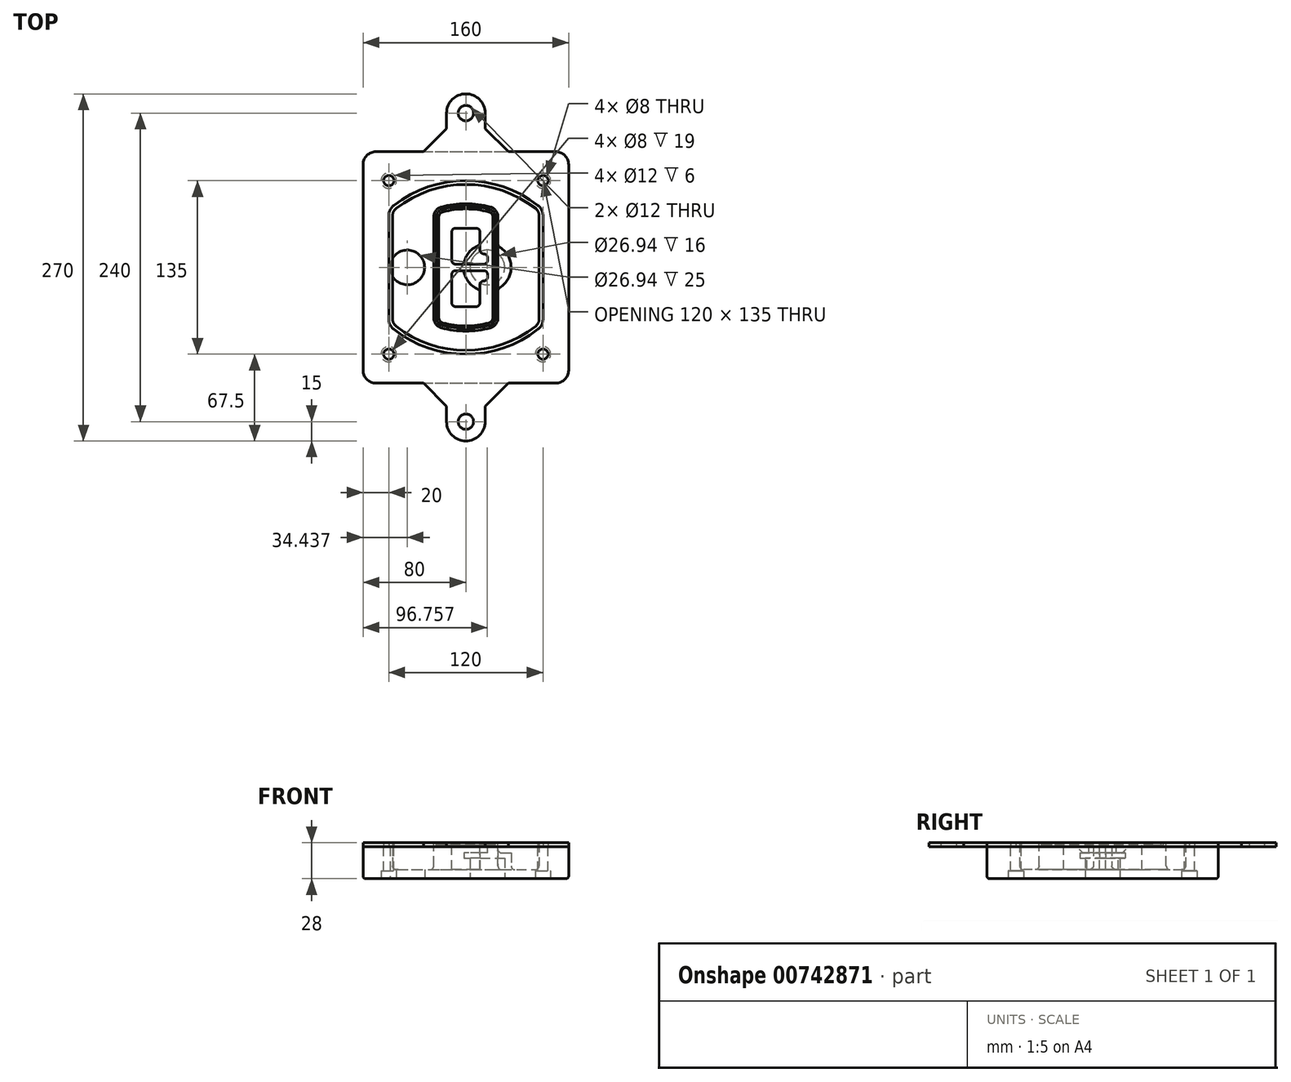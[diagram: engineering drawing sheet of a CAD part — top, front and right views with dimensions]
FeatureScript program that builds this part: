
annotation { "Feature Type Name" : "Feature", "Feature Type Description" : "" }
export const myFeature = defineFeature(function(context is Context, id is Id, definition is map)
    precondition{}
    {
        {
            var Q0;
            Q0=qCreatedBy(makeId("Top.planeOp"),FACE);
            var sketch = newSketch(context, id + "F0", { "sketchPlane" : qUnion([Q0])});
            skPoint(sketch, "E0.rect.middle", {"position": v(0, 0) * mm});
            skLineSegment(sketch, "E1.bottom", {"start": v(-70, -90) * mm, "end": v(70, -90) * mm});
            skLineSegment(sketch, "E1.top", {"start": v(-70, 90) * mm, "end": v(70, 90) * mm});
            skLineSegment(sketch, "E1.left", {"start": v(-80, -80) * mm, "end": v(-80, 80) * mm});
            skLineSegment(sketch, "E1.right", {"start": v(80, -80) * mm, "end": v(80, 80) * mm});
            skLineSegment(sketch, "E2", {"start": v(-80, 90) * mm, "end": v(80, -90) * mm, "construction": true});
            skLineSegment(sketch, "E3", {"start": v(80, 90) * mm, "end": v(-80, -90) * mm, "construction": true});
            skCircle(sketch, "E4", {"center": v(-60, 67.5) * mm, "radius": 4 * mm});
            skCircle(sketch, "E5", {"center": v(60, 67.5) * mm, "radius": 4 * mm});
            skCircle(sketch, "E6", {"center": v(60, -67.5) * mm, "radius": 4 * mm});
            skCircle(sketch, "E7", {"center": v(-60, -67.5) * mm, "radius": 4 * mm});
            skLineSegment(sketch, "E8", {"start": v(-60, 67.5) * mm, "end": v(60, 67.5) * mm, "construction": true});
            skLineSegment(sketch, "E9", {"start": v(60, 67.5) * mm, "end": v(60, -67.5) * mm, "construction": true});
            skLineSegment(sketch, "E10", {"start": v(60, -67.5) * mm, "end": v(-60, -67.5) * mm, "construction": true});
            skLineSegment(sketch, "E11", {"start": v(-60, -67.5) * mm, "end": v(-60, 67.5) * mm, "construction": true});
            skLineSegment(sketch, "E12", {"start": v(-60, 40.3) * mm, "end": v(-60, -40.3) * mm});
            skLineSegment(sketch, "E13", {"start": v(60, 40.3) * mm, "end": v(60, -40.3) * mm});
            skArc(sketch, "E14", {"start": v(56.15, 48.18) * mm, "mid": v(0, 67.5) * mm, "end": v(-56.15, 48.18) * mm});
            skArc(sketch, "E15", {"start": v(-56.15, -48.18) * mm, "mid": v(0, -67.5) * mm, "end": v(56.15, -48.18) * mm});
            skLineSegment(sketch, "E16", {"start": v(-60, 0) * mm, "end": v(60, 0) * mm, "construction": true});
            skPoint(sketch, "E17.visualSharp", {"position": v(-60, -45) * mm});
            skArc(sketch, "E17.filletArc", {"start": v(-60, -40.3) * mm, "mid": v(-58.99, -44.68) * mm, "end": v(-56.15, -48.18) * mm});
            skPoint(sketch, "E18.visualSharp", {"position": v(-60, 45) * mm});
            skArc(sketch, "E18.filletArc", {"start": v(-56.15, 48.18) * mm, "mid": v(-58.99, 44.68) * mm, "end": v(-60, 40.3) * mm});
            skPoint(sketch, "E19.visualSharp", {"position": v(60, 45) * mm});
            skArc(sketch, "E19.filletArc", {"start": v(60, 40.3) * mm, "mid": v(58.99, 44.68) * mm, "end": v(56.15, 48.18) * mm});
            skPoint(sketch, "E20.visualSharp", {"position": v(60, -45) * mm});
            skArc(sketch, "E20.filletArc", {"start": v(56.15, -48.18) * mm, "mid": v(58.99, -44.68) * mm, "end": v(60, -40.3) * mm});
            skPoint(sketch, "E21.visualSharp", {"position": v(-80, 90) * mm});
            skArc(sketch, "E21.filletArc", {"start": v(-70, 90) * mm, "mid": v(-77.07, 87.07) * mm, "end": v(-80, 80) * mm});
            skPoint(sketch, "E22.visualSharp", {"position": v(80, 90) * mm});
            skArc(sketch, "E22.filletArc", {"start": v(80, 80) * mm, "mid": v(77.07, 87.07) * mm, "end": v(70, 90) * mm});
            skPoint(sketch, "E23.visualSharp", {"position": v(80, -90) * mm});
            skArc(sketch, "E23.filletArc", {"start": v(70, -90) * mm, "mid": v(77.07, -87.07) * mm, "end": v(80, -80) * mm});
            skPoint(sketch, "E24.visualSharp", {"position": v(-80, -90) * mm});
            skArc(sketch, "E24.filletArc", {"start": v(-80, -80) * mm, "mid": v(-77.07, -87.07) * mm, "end": v(-70, -90) * mm});
            skArc(sketch, "E25.0", {"start": v(57, 40.3) * mm, "mid": v(56.3, 43.36) * mm, "end": v(54.3, 45.81) * mm});
            skLineSegment(sketch, "E25.1", {"start": v(57, 40.3) * mm, "end": v(57, -40.3) * mm});
            skArc(sketch, "E25.2", {"start": v(54.3, -45.81) * mm, "mid": v(56.3, -43.36) * mm, "end": v(57, -40.3) * mm});
            skArc(sketch, "E25.3", {"start": v(-54.3, -45.81) * mm, "mid": v(0, -64.5) * mm, "end": v(54.3, -45.81) * mm});
            skArc(sketch, "E25.4", {"start": v(-57, -40.3) * mm, "mid": v(-56.3, -43.36) * mm, "end": v(-54.3, -45.81) * mm});
            skArc(sketch, "E25.5", {"start": v(54.3, 45.81) * mm, "mid": v(0, 64.5) * mm, "end": v(-54.3, 45.81) * mm});
            skLineSegment(sketch, "E25.6", {"start": v(-57, 40.3) * mm, "end": v(-57, -40.3) * mm});
            skArc(sketch, "E25.7", {"start": v(-54.3, 45.81) * mm, "mid": v(-56.3, 43.36) * mm, "end": v(-57, 40.3) * mm});
            skArc(sketch, "E26.0", {"start": v(-58.62, 51.33) * mm, "mid": v(-62.58, 46.43) * mm, "end": v(-64, 40.3) * mm});
            skArc(sketch, "E26.1", {"start": v(58.62, 51.33) * mm, "mid": v(0, 71.5) * mm, "end": v(-58.62, 51.33) * mm});
            skArc(sketch, "E26.2", {"start": v(64, 40.3) * mm, "mid": v(62.58, 46.43) * mm, "end": v(58.62, 51.33) * mm});
            skLineSegment(sketch, "E26.3", {"start": v(64, 40.3) * mm, "end": v(64, -40.3) * mm});
            skArc(sketch, "E26.4", {"start": v(58.62, -51.33) * mm, "mid": v(62.58, -46.43) * mm, "end": v(64, -40.3) * mm});
            skLineSegment(sketch, "E26.5", {"start": v(-64, 40.3) * mm, "end": v(-64, -40.3) * mm});
            skArc(sketch, "E26.6", {"start": v(-58.62, -51.33) * mm, "mid": v(0, -71.5) * mm, "end": v(58.62, -51.33) * mm});
            skArc(sketch, "E26.7", {"start": v(-64, -40.3) * mm, "mid": v(-62.58, -46.43) * mm, "end": v(-58.62, -51.33) * mm});
            skSolve(sketch);
        }
        {
            var Q0;
            Q0=makeQuery(id+"F0.imprint","IMPRINT",FACE,{"disambiguationData":[TD([[makeQuery(id+"F0.imprint","IMPRINT",EDGE,{"derivedFrom":sQuery(id+"F0.wireOp",EDGE,"E1.bottom")}),1.0]])]});
            var Q1;
            Q1=makeQuery(id+"F0.imprint","IMPRINT",FACE,{"disambiguationData":[TD([[makeQuery(id+"F0.imprint","IMPRINT",EDGE,{"derivedFrom":sQuery(id+"F0.wireOp",EDGE,"E12")}),1.0]])]});
            var Q2;
            Q2=makeQuery(id+"F0.imprint","IMPRINT",FACE,{"disambiguationData":[TD([[makeQuery(id+"F0.imprint","IMPRINT",EDGE,{"derivedFrom":sQuery(id+"F0.wireOp",EDGE,"E25.0")}),1.0]])]});
            var Q3;
            Q3=makeQuery(id+"F0.imprint","IMPRINT",FACE,{"disambiguationData":[TD([[makeQuery(id+"F0.imprint","IMPRINT",EDGE,{"derivedFrom":sQuery(id+"F0.wireOp",EDGE,"E12")}),-1.0]])]});
            extrude(context, id + "F1", {"entities" : qUnion([Q0, Q1, Q2, Q3]), "oppositeDirection" : true, "depth" : 25 * mm});
        }
        {
            var Q0;
            Q0=makeQuery(id+"F0.imprint","IMPRINT",FACE,{"disambiguationData":[TD([[makeQuery(id+"F0.imprint","IMPRINT",EDGE,{"derivedFrom":sQuery(id+"F0.wireOp",EDGE,"E12")}),1.0]])]});
            extrude(context, id + "F2", {"entities" : qUnion([Q0]), "operationType" : NewBodyOperationType.ADD, "depth" : 3 * mm});
        }
        {
            var Q0;
            Q0=makeQuery(id+"F0.imprint","IMPRINT",FACE,{"disambiguationData":[TD([[makeQuery(id+"F0.imprint","IMPRINT",EDGE,{"derivedFrom":sQuery(id+"F0.wireOp",EDGE,"E25.0")}),1.0]])]});
            extrude(context, id + "F3", {"entities" : qUnion([Q0]), "operationType" : NewBodyOperationType.REMOVE, "oppositeDirection" : true, "depth" : 18 * mm});
        }
        {
            var Q0;
            Q0=makeQuery(id+"F2.opExtrude","CAP_FACE",FACE,{"disambiguationData":[OSD([sQuery(id+"F0.wireOp",EDGE,"E12"),sQuery(id+"F0.wireOp",EDGE,"E13"),sQuery(id+"F0.wireOp",EDGE,"E14"),sQuery(id+"F0.wireOp",EDGE,"E15"),sQuery(id+"F0.wireOp",EDGE,"E17.filletArc"),sQuery(id+"F0.wireOp",EDGE,"E18.filletArc"),sQuery(id+"F0.wireOp",EDGE,"E19.filletArc"),sQuery(id+"F0.wireOp",EDGE,"E20.filletArc"),sQuery(id+"F0.wireOp",EDGE,"E25.0"),sQuery(id+"F0.wireOp",EDGE,"E25.1"),sQuery(id+"F0.wireOp",EDGE,"E25.2"),sQuery(id+"F0.wireOp",EDGE,"E25.3"),sQuery(id+"F0.wireOp",EDGE,"E25.4"),sQuery(id+"F0.wireOp",EDGE,"E25.5"),sQuery(id+"F0.wireOp",EDGE,"E25.6"),sQuery(id+"F0.wireOp",EDGE,"E25.7")])],"isStart":false});
            var sketch = newSketch(context, id + "F4", { "sketchPlane" : qUnion([Q0])});
            skArc(sketch, "E27.0", {"start": v(-19.08, -46.97) * mm, "mid": v(0, -49.5) * mm, "end": v(19.08, -46.97) * mm});
            skArc(sketch, "E28.0", {"start": v(19.08, 46.97) * mm, "mid": v(0, 49.5) * mm, "end": v(-19.08, 46.97) * mm});
            skLineSegment(sketch, "E29", {"start": v(-25, 39.25) * mm, "end": v(-25, -39.25) * mm});
            skLineSegment(sketch, "E30", {"start": v(25, 39.25) * mm, "end": v(25, -39.25) * mm});
            skLineSegment(sketch, "E31", {"start": v(-25, 45.1) * mm, "end": v(25, 45.1) * mm, "construction": true});
            skLineSegment(sketch, "E32", {"start": v(-25, -45.1) * mm, "end": v(25, -45.1) * mm, "construction": true});
            skPoint(sketch, "E33.visualSharp", {"position": v(-25, 45.1) * mm});
            skArc(sketch, "E33.filletArc", {"start": v(-19.08, 46.97) * mm, "mid": v(-23.35, 44.11) * mm, "end": v(-25, 39.25) * mm});
            skPoint(sketch, "E34.visualSharp", {"position": v(25, 45.1) * mm});
            skArc(sketch, "E34.filletArc", {"start": v(25, 39.25) * mm, "mid": v(23.35, 44.11) * mm, "end": v(19.08, 46.97) * mm});
            skPoint(sketch, "E35.visualSharp", {"position": v(25, -45.1) * mm});
            skArc(sketch, "E35.filletArc", {"start": v(19.08, -46.97) * mm, "mid": v(23.35, -44.11) * mm, "end": v(25, -39.25) * mm});
            skPoint(sketch, "E36.visualSharp", {"position": v(-25, -45.1) * mm});
            skArc(sketch, "E36.filletArc", {"start": v(-25, -39.25) * mm, "mid": v(-23.35, -44.11) * mm, "end": v(-19.08, -46.97) * mm});
            skArc(sketch, "E37.0", {"start": v(54.3, 45.81) * mm, "mid": v(0, 64.5) * mm, "end": v(-54.3, 45.81) * mm});
            skArc(sketch, "E37.1", {"start": v(-54.3, 45.81) * mm, "mid": v(-56.3, 43.36) * mm, "end": v(-57, 40.3) * mm});
            skLineSegment(sketch, "E37.2", {"start": v(-57, 40.3) * mm, "end": v(-57, -40.3) * mm});
            skArc(sketch, "E37.3", {"start": v(-57, -40.3) * mm, "mid": v(-56.3, -43.36) * mm, "end": v(-54.3, -45.81) * mm});
            skArc(sketch, "E37.4", {"start": v(-54.3, -45.81) * mm, "mid": v(0, -64.5) * mm, "end": v(54.3, -45.81) * mm});
            skArc(sketch, "E37.5", {"start": v(54.3, -45.81) * mm, "mid": v(56.3, -43.36) * mm, "end": v(57, -40.3) * mm});
            skLineSegment(sketch, "E37.6", {"start": v(57, 40.3) * mm, "end": v(57, -40.3) * mm});
            skArc(sketch, "E37.7", {"start": v(57, 40.3) * mm, "mid": v(56.3, 43.36) * mm, "end": v(54.3, 45.81) * mm});
            skLineSegment(sketch, "E38.0", {"start": v(23, 39.25) * mm, "end": v(23, -39.25) * mm});
            skArc(sketch, "E38.1", {"start": v(18.56, -45.04) * mm, "mid": v(21.76, -42.9) * mm, "end": v(23, -39.25) * mm});
            skArc(sketch, "E38.2", {"start": v(-18.56, -45.04) * mm, "mid": v(0, -47.5) * mm, "end": v(18.56, -45.04) * mm});
            skArc(sketch, "E38.3", {"start": v(-23, -39.25) * mm, "mid": v(-21.76, -42.9) * mm, "end": v(-18.56, -45.04) * mm});
            skLineSegment(sketch, "E38.4", {"start": v(-23, 39.25) * mm, "end": v(-23, -39.25) * mm});
            skArc(sketch, "E38.5", {"start": v(23, 39.25) * mm, "mid": v(21.76, 42.9) * mm, "end": v(18.56, 45.04) * mm});
            skArc(sketch, "E38.6", {"start": v(-18.56, 45.04) * mm, "mid": v(-21.76, 42.9) * mm, "end": v(-23, 39.25) * mm});
            skArc(sketch, "E38.7", {"start": v(18.56, 45.04) * mm, "mid": v(0, 47.5) * mm, "end": v(-18.56, 45.04) * mm});
            skArc(sketch, "E39.0", {"start": v(21, 39.25) * mm, "mid": v(20.18, 41.68) * mm, "end": v(18.04, 43.1) * mm});
            skLineSegment(sketch, "E39.1", {"start": v(21, 39.25) * mm, "end": v(21, -39.25) * mm});
            skArc(sketch, "E39.2", {"start": v(18.04, -43.1) * mm, "mid": v(20.18, -41.68) * mm, "end": v(21, -39.25) * mm});
            skArc(sketch, "E39.3", {"start": v(-18.04, -43.1) * mm, "mid": v(0, -45.5) * mm, "end": v(18.04, -43.1) * mm});
            skArc(sketch, "E39.4", {"start": v(-21, -39.25) * mm, "mid": v(-20.18, -41.68) * mm, "end": v(-18.04, -43.1) * mm});
            skArc(sketch, "E39.5", {"start": v(18.04, 43.1) * mm, "mid": v(0, 45.5) * mm, "end": v(-18.04, 43.1) * mm});
            skLineSegment(sketch, "E39.6", {"start": v(-21, 39.25) * mm, "end": v(-21, -39.25) * mm});
            skArc(sketch, "E39.7", {"start": v(-18.04, 43.1) * mm, "mid": v(-20.18, 41.68) * mm, "end": v(-21, 39.25) * mm});
            skLineSegment(sketch, "E40", {"start": v(-25, 0) * mm, "end": v(25, 0) * mm, "construction": true});
            skLineSegment(sketch, "E41", {"start": v(-11, 5.5) * mm, "end": v(-11, 27.5) * mm});
            skLineSegment(sketch, "E42", {"start": v(-8, 30.5) * mm, "end": v(8, 30.5) * mm});
            skLineSegment(sketch, "E43", {"start": v(11, 27.5) * mm, "end": v(11, 13.5) * mm});
            skLineSegment(sketch, "E44", {"start": v(14, 10.5) * mm, "end": v(14, 10.5) * mm});
            skLineSegment(sketch, "E45", {"start": v(17, 7.5) * mm, "end": v(17, 5.5) * mm});
            skLineSegment(sketch, "E46", {"start": v(14, 2.5) * mm, "end": v(-8, 2.5) * mm});
            skPoint(sketch, "E47.visualSharp", {"position": v(-11, 30.5) * mm});
            skArc(sketch, "E47.filletArc", {"start": v(-8, 30.5) * mm, "mid": v(-10.12, 29.62) * mm, "end": v(-11, 27.5) * mm});
            skPoint(sketch, "E48.visualSharp", {"position": v(11, 30.5) * mm});
            skArc(sketch, "E48.filletArc", {"start": v(11, 27.5) * mm, "mid": v(10.12, 29.62) * mm, "end": v(8, 30.5) * mm});
            skPoint(sketch, "E49.visualSharp", {"position": v(11, 10.5) * mm});
            skArc(sketch, "E49.filletArc", {"start": v(11, 13.5) * mm, "mid": v(11.88, 11.38) * mm, "end": v(14, 10.5) * mm});
            skPoint(sketch, "E50.visualSharp", {"position": v(17, 10.5) * mm});
            skArc(sketch, "E50.filletArc", {"start": v(17, 7.5) * mm, "mid": v(16.12, 9.62) * mm, "end": v(14, 10.5) * mm});
            skPoint(sketch, "E51.visualSharp", {"position": v(17, 2.5) * mm});
            skArc(sketch, "E51.filletArc", {"start": v(14, 2.5) * mm, "mid": v(16.12, 3.38) * mm, "end": v(17, 5.5) * mm});
            skPoint(sketch, "E52.visualSharp", {"position": v(-11, 2.5) * mm});
            skArc(sketch, "E52.filletArc", {"start": v(-11, 5.5) * mm, "mid": v(-10.12, 3.38) * mm, "end": v(-8, 2.5) * mm});
            skLineSegment(sketch, "E53.0.MirrorCS", {"start": v(14, -2.5) * mm, "end": v(-8, -2.5) * mm});
            skArc(sketch, "E54.0.MirrorCS", {"start": v(-11, -5.5) * mm, "mid": v(-10.12, -3.38) * mm, "end": v(-8, -2.5) * mm});
            skLineSegment(sketch, "E55.0.MirrorCS", {"start": v(-11, -5.5) * mm, "end": v(-11, -27.5) * mm});
            skArc(sketch, "E56.0.MirrorCS", {"start": v(-8, -30.5) * mm, "mid": v(-10.12, -29.62) * mm, "end": v(-11, -27.5) * mm});
            skLineSegment(sketch, "E57.0.MirrorCS", {"start": v(-8, -30.5) * mm, "end": v(8, -30.5) * mm});
            skArc(sketch, "E58.0.MirrorCS", {"start": v(11, -27.5) * mm, "mid": v(10.12, -29.62) * mm, "end": v(8, -30.5) * mm});
            skLineSegment(sketch, "E59.0.MirrorCS", {"start": v(11, -27.5) * mm, "end": v(11, -13.5) * mm});
            skArc(sketch, "E60.0.MirrorCS", {"start": v(11, -13.5) * mm, "mid": v(11.88, -11.38) * mm, "end": v(14, -10.5) * mm});
            skArc(sketch, "E61.0.MirrorCS", {"start": v(17, -7.5) * mm, "mid": v(16.12, -9.62) * mm, "end": v(14, -10.5) * mm});
            skLineSegment(sketch, "E62.0.MirrorCS", {"start": v(17, -7.5) * mm, "end": v(17, -5.5) * mm});
            skArc(sketch, "E63.0.MirrorCS", {"start": v(14, -2.5) * mm, "mid": v(16.12, -3.38) * mm, "end": v(17, -5.5) * mm});
            skSolve(sketch);
        }
        {
            var Q0;
            Q0=makeQuery(id+"F4.imprint","IMPRINT",FACE,{"disambiguationData":[TD([[makeQuery(id+"F4.imprint","IMPRINT",EDGE,{"derivedFrom":sQuery(id+"F4.wireOp",EDGE,"E27.0")}),1.0]])]});
            var Q1;
            Q1=makeQuery(id+"F4.imprint","IMPRINT",FACE,{"disambiguationData":[TD([[makeQuery(id+"F4.imprint","IMPRINT",EDGE,{"derivedFrom":sQuery(id+"F4.wireOp",EDGE,"E38.0")}),-1.0]])]});
            var Q2;
            Q2=makeQuery(id+"F4.imprint","IMPRINT",FACE,{"disambiguationData":[TD([[makeQuery(id+"F4.imprint","IMPRINT",EDGE,{"derivedFrom":sQuery(id+"F4.wireOp",EDGE,"E39.0")}),1.0]])]});
            extrude(context, id + "F5", {"entities" : qUnion([Q0, Q1, Q2]), "operationType" : NewBodyOperationType.ADD, "endBound" : BoundingType.UP_TO_NEXT, "oppositeDirection" : true, "depth" : 25 * mm});
        }
        {
            var Q0;
            Q0=makeQuery(id+"F4.imprint","IMPRINT",FACE,{"disambiguationData":[TD([[makeQuery(id+"F4.imprint","IMPRINT",EDGE,{"derivedFrom":sQuery(id+"F4.wireOp",EDGE,"E38.0")}),-1.0]])]});
            extrude(context, id + "F6", {"entities" : qUnion([Q0]), "operationType" : NewBodyOperationType.REMOVE, "oppositeDirection" : true, "depth" : 2 * mm});
        }
        {
            var Q0;
            Q0=makeQuery(id+"F1.opExtrude","CAP_FACE",FACE,{"disambiguationData":[OSD([sQuery(id+"F0.wireOp",EDGE,"E1.bottom"),sQuery(id+"F0.wireOp",EDGE,"E1.top"),sQuery(id+"F0.wireOp",EDGE,"E1.left"),sQuery(id+"F0.wireOp",EDGE,"E1.right"),sQuery(id+"F0.wireOp",EDGE,"E4"),sQuery(id+"F0.wireOp",EDGE,"E5"),sQuery(id+"F0.wireOp",EDGE,"E6"),sQuery(id+"F0.wireOp",EDGE,"E7"),sQuery(id+"F0.wireOp",EDGE,"E21.filletArc"),sQuery(id+"F0.wireOp",EDGE,"E22.filletArc"),sQuery(id+"F0.wireOp",EDGE,"E23.filletArc"),sQuery(id+"F0.wireOp",EDGE,"E24.filletArc")])],"isStart":false});
            var sketch = newSketch(context, id + "F7", { "sketchPlane" : qUnion([Q0])});
            skCircle(sketch, "E64", {"center": v(16.76, 0) * mm, "radius": 13.47 * mm});
            skCircle(sketch, "E65", {"center": v(-45.56, 0) * mm, "radius": 13.47 * mm});
            skLineSegment(sketch, "E66", {"start": v(80, 0) * mm, "end": v(-80, 0) * mm});
            skCircle(sketch, "E67", {"center": v(16.76, 0) * mm, "radius": 18.47 * mm});
            skCircle(sketch, "E68", {"center": v(60, -67.5) * mm, "radius": 6 * mm});
            skCircle(sketch, "E69", {"center": v(-60, -67.5) * mm, "radius": 6 * mm});
            skCircle(sketch, "E70", {"center": v(-60, 67.5) * mm, "radius": 6 * mm});
            skCircle(sketch, "E71", {"center": v(60, 67.5) * mm, "radius": 6 * mm});
            skSolve(sketch);
        }
        {
            var Q0;
            {var subQ1=sQuery(id+"F7.wireOp",EDGE,"E66");var subQ4=sQuery(id+"F7.wireOp",EDGE,"E64");var subQ6=makeQuery(id+"F7.imprint","INTERSECT",VERTEX,{"disambiguationData":[OD(0.0)],"derivedFrom":[subQ4,subQ1]});Q0=makeQuery(id+"F7.imprint","IMPRINT",FACE,{"disambiguationData":[TD([[makeQuery(id+"F7.imprint","IMPRINT",EDGE,{"disambiguationData":[TD([[subQ6,-1.0]])],"derivedFrom":subQ4}),-1.0]])]});}
            var Q1;
            {var subQ0=sQuery(id+"F7.wireOp",EDGE,"E66");var subQ1=sQuery(id+"F7.wireOp",EDGE,"E64");var subQ3=makeQuery(id+"F7.imprint","INTERSECT",VERTEX,{"disambiguationData":[OD(0.0)],"derivedFrom":[subQ1,subQ0]});Q1=makeQuery(id+"F7.imprint","IMPRINT",FACE,{"disambiguationData":[TD([[makeQuery(id+"F7.imprint","IMPRINT",EDGE,{"disambiguationData":[TD([[subQ3,-1.0]])],"derivedFrom":subQ1}),1.0]])]});}
            var Q2;
            {var subQ0=sQuery(id+"F7.wireOp",EDGE,"E66");var subQ1=sQuery(id+"F7.wireOp",EDGE,"E64");var subQ3=makeQuery(id+"F7.imprint","INTERSECT",VERTEX,{"disambiguationData":[OD(0.0)],"derivedFrom":[subQ1,subQ0]});Q2=makeQuery(id+"F7.imprint","IMPRINT",FACE,{"disambiguationData":[TD([[makeQuery(id+"F7.imprint","IMPRINT",EDGE,{"disambiguationData":[TD([[subQ3,1.0]])],"derivedFrom":subQ1}),1.0]])]});}
            var Q3;
            {var subQ1=sQuery(id+"F7.wireOp",EDGE,"E66");var subQ4=sQuery(id+"F7.wireOp",EDGE,"E64");var subQ6=makeQuery(id+"F7.imprint","INTERSECT",VERTEX,{"disambiguationData":[OD(0.0)],"derivedFrom":[subQ4,subQ1]});Q3=makeQuery(id+"F7.imprint","IMPRINT",FACE,{"disambiguationData":[TD([[makeQuery(id+"F7.imprint","IMPRINT",EDGE,{"disambiguationData":[TD([[subQ6,1.0]])],"derivedFrom":subQ4}),-1.0]])]});}
            extrude(context, id + "F8", {"entities" : qUnion([Q0, Q1, Q2, Q3]), "operationType" : NewBodyOperationType.ADD, "oppositeDirection" : true, "depth" : 20 * mm});
        }
        {
            var Q0;
            {var subQ0=sQuery(id+"F7.wireOp",EDGE,"E66");var subQ1=sQuery(id+"F7.wireOp",EDGE,"E64");var subQ3=makeQuery(id+"F7.imprint","INTERSECT",VERTEX,{"disambiguationData":[OD(0.0)],"derivedFrom":[subQ1,subQ0]});Q0=makeQuery(id+"F7.imprint","IMPRINT",FACE,{"disambiguationData":[TD([[makeQuery(id+"F7.imprint","IMPRINT",EDGE,{"disambiguationData":[TD([[subQ3,-1.0]])],"derivedFrom":subQ1}),1.0]])]});}
            var Q1;
            {var subQ0=sQuery(id+"F7.wireOp",EDGE,"E66");var subQ1=sQuery(id+"F7.wireOp",EDGE,"E64");var subQ3=makeQuery(id+"F7.imprint","INTERSECT",VERTEX,{"disambiguationData":[OD(0.0)],"derivedFrom":[subQ1,subQ0]});Q1=makeQuery(id+"F7.imprint","IMPRINT",FACE,{"disambiguationData":[TD([[makeQuery(id+"F7.imprint","IMPRINT",EDGE,{"disambiguationData":[TD([[subQ3,1.0]])],"derivedFrom":subQ1}),1.0]])]});}
            extrude(context, id + "F9", {"entities" : qUnion([Q0, Q1]), "operationType" : NewBodyOperationType.REMOVE, "oppositeDirection" : true, "depth" : 16 * mm});
        }
        {
            var Q0;
            {var subQ0=sQuery(id+"F7.wireOp",EDGE,"E66");var subQ1=sQuery(id+"F7.wireOp",EDGE,"E65");var subQ3=makeQuery(id+"F7.imprint","INTERSECT",VERTEX,{"disambiguationData":[OD(0.0)],"derivedFrom":[subQ1,subQ0]});Q0=makeQuery(id+"F7.imprint","IMPRINT",FACE,{"disambiguationData":[TD([[makeQuery(id+"F7.imprint","IMPRINT",EDGE,{"disambiguationData":[TD([[subQ3,-1.0]])],"derivedFrom":subQ1}),1.0]])]});}
            var Q1;
            {var subQ0=sQuery(id+"F7.wireOp",EDGE,"E66");var subQ1=sQuery(id+"F7.wireOp",EDGE,"E65");var subQ3=makeQuery(id+"F7.imprint","INTERSECT",VERTEX,{"disambiguationData":[OD(0.0)],"derivedFrom":[subQ1,subQ0]});Q1=makeQuery(id+"F7.imprint","IMPRINT",FACE,{"disambiguationData":[TD([[makeQuery(id+"F7.imprint","IMPRINT",EDGE,{"disambiguationData":[TD([[subQ3,1.0]])],"derivedFrom":subQ1}),1.0]])]});}
            extrude(context, id + "F10", {"entities" : qUnion([Q0, Q1]), "operationType" : NewBodyOperationType.REMOVE, "oppositeDirection" : true, "depth" : 25 * mm});
        }
        {
            var Q0;
            Q0=makeQuery(id+"F7.imprint","IMPRINT",FACE,{"disambiguationData":[TD([[makeQuery(id+"F7.imprint","IMPRINT",EDGE,{"derivedFrom":sQuery(id+"F7.wireOp",EDGE,"E68")}),1.0]])]});
            var Q1;
            Q1=makeQuery(id+"F7.imprint","IMPRINT",FACE,{"disambiguationData":[TD([[makeQuery(id+"F7.imprint","IMPRINT",EDGE,{"derivedFrom":makeQuery(id+"F1.opExtrude","CAP_EDGE",EDGE,{"disambiguationData":[OSD([sQuery(id+"F0.wireOp",EDGE,"E5")])],"isStart":false})}),-1.0]])]});
            var Q2;
            Q2=makeQuery(id+"F7.imprint","IMPRINT",FACE,{"disambiguationData":[TD([[makeQuery(id+"F7.imprint","IMPRINT",EDGE,{"derivedFrom":sQuery(id+"F7.wireOp",EDGE,"E69")}),1.0]])]});
            var Q3;
            Q3=makeQuery(id+"F7.imprint","IMPRINT",FACE,{"disambiguationData":[TD([[makeQuery(id+"F7.imprint","IMPRINT",EDGE,{"derivedFrom":makeQuery(id+"F1.opExtrude","CAP_EDGE",EDGE,{"disambiguationData":[OSD([sQuery(id+"F0.wireOp",EDGE,"E4")])],"isStart":false})}),-1.0]])]});
            var Q4;
            Q4=makeQuery(id+"F7.imprint","IMPRINT",FACE,{"disambiguationData":[TD([[makeQuery(id+"F7.imprint","IMPRINT",EDGE,{"derivedFrom":sQuery(id+"F7.wireOp",EDGE,"E70")}),1.0]])]});
            var Q5;
            Q5=makeQuery(id+"F7.imprint","IMPRINT",FACE,{"disambiguationData":[TD([[makeQuery(id+"F7.imprint","IMPRINT",EDGE,{"derivedFrom":makeQuery(id+"F1.opExtrude","CAP_EDGE",EDGE,{"disambiguationData":[OSD([sQuery(id+"F0.wireOp",EDGE,"E7")])],"isStart":false})}),-1.0]])]});
            var Q6;
            Q6=makeQuery(id+"F7.imprint","IMPRINT",FACE,{"disambiguationData":[TD([[makeQuery(id+"F7.imprint","IMPRINT",EDGE,{"derivedFrom":sQuery(id+"F7.wireOp",EDGE,"E71")}),1.0]])]});
            var Q7;
            Q7=makeQuery(id+"F7.imprint","IMPRINT",FACE,{"disambiguationData":[TD([[makeQuery(id+"F7.imprint","IMPRINT",EDGE,{"derivedFrom":makeQuery(id+"F1.opExtrude","CAP_EDGE",EDGE,{"disambiguationData":[OSD([sQuery(id+"F0.wireOp",EDGE,"E6")])],"isStart":false})}),-1.0]])]});
            extrude(context, id + "F11", {"entities" : qUnion([Q0, Q1, Q2, Q3, Q4, Q5, Q6, Q7]), "operationType" : NewBodyOperationType.REMOVE, "oppositeDirection" : true, "depth" : 6 * mm});
        }
        {
            var Q0;
            Q0=makeQuery(id+"F9.boolean.opBoolean","COPY",FACE,{"derivedFrom":makeQuery(id+"F9.opExtrude","CAP_FACE",FACE,{"disambiguationData":[OSD([sQuery(id+"F7.wireOp",EDGE,"E64")])],"isStart":false})});
            var sketch = newSketch(context, id + "F12", { "sketchPlane" : qUnion([Q0])});
            skArc(sketch, "E72.0", {"start": v(11, 17.55) * mm, "mid": v(2.57, 11.82) * mm, "end": v(-1.54, 2.5) * mm});
            skArc(sketch, "E72.1", {"start": v(-1.54, -2.5) * mm, "mid": v(2.57, -11.82) * mm, "end": v(11, -17.55) * mm});
            skLineSegment(sketch, "E73", {"start": v(-1.54, -2.5) * mm, "end": v(14, -2.5) * mm});
            skLineSegment(sketch, "E74.0", {"start": v(14, 2.5) * mm, "end": v(-1.54, 2.5) * mm});
            skArc(sketch, "E74.1", {"start": v(14, 2.5) * mm, "mid": v(16.12, 3.38) * mm, "end": v(17, 5.5) * mm});
            skLineSegment(sketch, "E74.2", {"start": v(17, 7.5) * mm, "end": v(17, 5.5) * mm});
            skArc(sketch, "E74.3", {"start": v(17, 7.5) * mm, "mid": v(16.12, 9.62) * mm, "end": v(14, 10.5) * mm});
            skArc(sketch, "E74.4", {"start": v(11, 13.5) * mm, "mid": v(11.88, 11.38) * mm, "end": v(14, 10.5) * mm});
            skLineSegment(sketch, "E74.5", {"start": v(11, 17.55) * mm, "end": v(11, 13.5) * mm});
            skLineSegment(sketch, "E74.7", {"start": v(14, -2.5) * mm, "end": v(-1.54, -2.5) * mm});
            skArc(sketch, "E74.8", {"start": v(14, -2.5) * mm, "mid": v(16.12, -3.38) * mm, "end": v(17, -5.5) * mm});
            skLineSegment(sketch, "E74.9", {"start": v(17, -7.5) * mm, "end": v(17, -5.5) * mm});
            skArc(sketch, "E74.10", {"start": v(17, -7.5) * mm, "mid": v(16.12, -9.62) * mm, "end": v(14, -10.5) * mm});
            skArc(sketch, "E74.11", {"start": v(11, -13.5) * mm, "mid": v(11.88, -11.38) * mm, "end": v(14, -10.5) * mm});
            skLineSegment(sketch, "E74.12", {"start": v(11, -17.55) * mm, "end": v(11, -13.5) * mm});
            skPoint(sketch, "E75.orphan", {"position": v(11, -27.5) * mm});
            skPoint(sketch, "E76.orphan", {"position": v(-8, -2.5) * mm});
            skPoint(sketch, "E77.orphan", {"position": v(-8, 2.5) * mm});
            skPoint(sketch, "E78.orphan", {"position": v(11, 27.5) * mm});
            skSolve(sketch);
        }
        {
            var Q0;
            {var subQ7=sQuery(id+"F12.wireOp",EDGE,"E72.0");var subQ14=sQuery(id+"F12.wireOp",EDGE,"E72.1");var subQ16=sQuery(id+"F12.wireOp",EDGE,"E74.1");var subQ18=sQuery(id+"F12.wireOp",EDGE,"E74.8");Q0=qUnion([makeQuery(id+"F12.imprint","IMPRINT",FACE,{"disambiguationData":[TD([[makeQuery(id+"F12.imprint","IMPRINT",EDGE,{"derivedFrom":subQ7}),1.0]])]}),makeQuery(id+"F12.imprint","IMPRINT",FACE,{"disambiguationData":[TD([[makeQuery(id+"F12.imprint","IMPRINT",EDGE,{"derivedFrom":subQ14}),1.0]])]}),makeQuery(id+"F12.imprint","IMPRINT",FACE,{"disambiguationData":[TD([[makeQuery(id+"F12.imprint","IMPRINT",EDGE,{"derivedFrom":subQ16}),1.0]])]}),makeQuery(id+"F12.imprint","IMPRINT",FACE,{"disambiguationData":[TD([[makeQuery(id+"F12.imprint","IMPRINT",EDGE,{"derivedFrom":subQ18}),-1.0]])]})]);}
            var Q1;
            Q1=makeQuery(id+"F5.boolean.opBoolean","SPLIT",FACE,{"disambiguationData":[TD([makeQuery(id+"F5.opExtrude","SWEPT_FACE",FACE,{"disambiguationData":[OSD([sQuery(id+"F4.wireOp",EDGE,"E41")])]})])],"derivedFrom":makeQuery(id+"F3.boolean.opBoolean","COPY",FACE,{"derivedFrom":makeQuery(id+"F3.opExtrude","CAP_FACE",FACE,{"disambiguationData":[OSD([sQuery(id+"F0.wireOp",EDGE,"E25.0"),sQuery(id+"F0.wireOp",EDGE,"E25.1"),sQuery(id+"F0.wireOp",EDGE,"E25.2"),sQuery(id+"F0.wireOp",EDGE,"E25.3"),sQuery(id+"F0.wireOp",EDGE,"E25.4"),sQuery(id+"F0.wireOp",EDGE,"E25.5"),sQuery(id+"F0.wireOp",EDGE,"E25.6"),sQuery(id+"F0.wireOp",EDGE,"E25.7")])],"isStart":false})})});
            extrude(context, id + "F13", {"entities" : qUnion([Q0]), "operationType" : NewBodyOperationType.REMOVE, "endBound" : BoundingType.UP_TO_SURFACE, "endBoundEntityFace" : qUnion([Q1]), "depth" : 25 * mm});
        }
        {
            var Q0;
            Q0=makeQuery(id+"F3.boolean.opBoolean","COPY",EDGE,{"derivedFrom":makeQuery(id+"F3.opExtrude","CAP_EDGE",EDGE,{"disambiguationData":[OSD([sQuery(id+"F0.wireOp",EDGE,"E25.6")])],"isStart":false})});
            var Q1;
            Q1=makeQuery(id+"F8.boolean.opBoolean","INTERSECT",EDGE,{"derivedFrom":[makeQuery(id+"F5.opExtrude","SWEPT_FACE",FACE,{"disambiguationData":[OSD([sQuery(id+"F4.wireOp",EDGE,"E30")])]}),makeQuery(id+"F8.opExtrude","CAP_FACE",FACE,{"disambiguationData":[OSD([sQuery(id+"F7.wireOp",EDGE,"E67")])],"isStart":false})]});
            var Q2;
            Q2=makeQuery(id+"F8.boolean.opBoolean","INTERSECT",EDGE,{"disambiguationData":[OD(1.0)],"derivedFrom":[makeQuery(id+"F5.opExtrude","SWEPT_FACE",FACE,{"disambiguationData":[OSD([sQuery(id+"F4.wireOp",EDGE,"E30")])]}),makeQuery(id+"F8.opExtrude","SWEPT_FACE",FACE,{"disambiguationData":[OSD([sQuery(id+"F7.wireOp",EDGE,"E67")])]})]});
            var Q3;
            {var subQ0=sQuery(id+"F4.wireOp",EDGE,"E30");Q3=makeQuery(id+"F8.boolean.opBoolean","SPLIT",EDGE,{"disambiguationData":[TD([makeQuery(id+"F5.opExtrude","SWEPT_FACE",FACE,{"disambiguationData":[OSD([sQuery(id+"F4.wireOp",EDGE,"E35.filletArc")])]})])],"derivedFrom":makeQuery(id+"F5.opExtrude","CAP_EDGE",EDGE,{"disambiguationData":[OSD([subQ0])],"isStart":false})});}
            var Q4;
            {var subQ0=sQuery(id+"F0.wireOp",EDGE,"E25.7");var subQ1=sQuery(id+"F0.wireOp",EDGE,"E25.1");var subQ2=sQuery(id+"F0.wireOp",EDGE,"E25.6");var subQ3=sQuery(id+"F0.wireOp",EDGE,"E25.5");var subQ4=sQuery(id+"F0.wireOp",EDGE,"E25.4");var subQ5=sQuery(id+"F0.wireOp",EDGE,"E25.0");var subQ6=sQuery(id+"F0.wireOp",EDGE,"E25.2");var subQ7=sQuery(id+"F0.wireOp",EDGE,"E25.3");Q4=makeQuery(id+"F8.boolean.opBoolean","INTERSECT",EDGE,{"derivedFrom":[makeQuery(id+"F5.boolean.opBoolean","SPLIT",FACE,{"disambiguationData":[TD([makeQuery(id+"F2.opExtrude","SWEPT_FACE",FACE,{"disambiguationData":[OSD([subQ5])]})])],"derivedFrom":makeQuery(id+"F3.boolean.opBoolean","COPY",FACE,{"derivedFrom":makeQuery(id+"F3.opExtrude","CAP_FACE",FACE,{"disambiguationData":[OSD([subQ5,subQ1,subQ6,subQ7,subQ4,subQ3,subQ2,subQ0])],"isStart":false})})}),makeQuery(id+"F8.opExtrude","SWEPT_FACE",FACE,{"disambiguationData":[OSD([sQuery(id+"F7.wireOp",EDGE,"E67")])]})]});}
            var Q5;
            Q5=makeQuery(id+"F8.boolean.opBoolean","INTERSECT",EDGE,{"disambiguationData":[OD(0.0)],"derivedFrom":[makeQuery(id+"F5.opExtrude","SWEPT_FACE",FACE,{"disambiguationData":[OSD([sQuery(id+"F4.wireOp",EDGE,"E30")])]}),makeQuery(id+"F8.opExtrude","SWEPT_FACE",FACE,{"disambiguationData":[OSD([sQuery(id+"F7.wireOp",EDGE,"E67")])]})]});
            fillet(context, id + "F14", {"entities" : qUnion([Q0, Q1, Q2, Q3, Q4, Q5]), "radius" : 3 * mm, "tangentPropagation" : true, "allowEdgeOverflow" : false});
        }
        {
            var Q0;
            Q0=makeQuery(id+"F1.opExtrude","CAP_EDGE",EDGE,{"disambiguationData":[OSD([sQuery(id+"F0.wireOp",EDGE,"E1.bottom")])],"isStart":false});
            fillet(context, id + "F15", {"entities" : qUnion([Q0]), "radius" : 2 * mm, "tangentPropagation" : true, "allowEdgeOverflow" : false});
        }
        {
            var Q0;
            {var subQ0=sQuery(id+"F0.wireOp",EDGE,"E21.filletArc");var subQ1=sQuery(id+"F0.wireOp",EDGE,"E7");var subQ2=sQuery(id+"F0.wireOp",EDGE,"E6");var subQ3=sQuery(id+"F0.wireOp",EDGE,"E5");var subQ4=sQuery(id+"F0.wireOp",EDGE,"E4");var subQ5=sQuery(id+"F0.wireOp",EDGE,"E22.filletArc");var subQ6=sQuery(id+"F0.wireOp",EDGE,"E1.bottom");var subQ7=sQuery(id+"F0.wireOp",EDGE,"E1.right");var subQ8=sQuery(id+"F0.wireOp",EDGE,"E1.top");var subQ9=sQuery(id+"F0.wireOp",EDGE,"E1.left");var subQ10=sQuery(id+"F0.wireOp",EDGE,"E23.filletArc");var subQ11=sQuery(id+"F0.wireOp",EDGE,"E24.filletArc");Q0=makeQuery(id+"F2.boolean.opBoolean","SPLIT",FACE,{"disambiguationData":[TD([makeQuery(id+"F1.opExtrude","SWEPT_FACE",FACE,{"disambiguationData":[OSD([subQ6])]})])],"derivedFrom":makeQuery(id+"F1.opExtrude","CAP_FACE",FACE,{"disambiguationData":[OSD([subQ6,subQ8,subQ9,subQ7,subQ4,subQ3,subQ2,subQ1,subQ0,subQ5,subQ10,subQ11])],"isStart":true})});}
            var sketch = newSketch(context, id + "F16", { "sketchPlane" : qUnion([Q0])});
            skLineSegment(sketch, "E79", {"start": v(-33, 90) * mm, "end": v(-15, 108) * mm});
            skLineSegment(sketch, "E80", {"start": v(-15, 108) * mm, "end": v(-15, 120) * mm});
            skLineSegment(sketch, "E81", {"start": v(33, 90) * mm, "end": v(15, 108) * mm});
            skLineSegment(sketch, "E82", {"start": v(15, 108) * mm, "end": v(15, 120) * mm});
            skArc(sketch, "E83", {"start": v(15, 120) * mm, "mid": v(0, 135) * mm, "end": v(-15, 120) * mm});
            skCircle(sketch, "E84", {"center": v(0, 120) * mm, "radius": 6 * mm});
            skLineSegment(sketch, "E85", {"start": v(0, 90) * mm, "end": v(0, 120) * mm, "construction": true});
            skLineSegment(sketch, "E86", {"start": v(-80, 0) * mm, "end": v(80, 0) * mm, "construction": true});
            skLineSegment(sketch, "E87.MirrorCS", {"start": v(-33, -90) * mm, "end": v(-15, -108) * mm});
            skLineSegment(sketch, "E88.MirrorCS", {"start": v(-15, -108) * mm, "end": v(-15, -120) * mm});
            skArc(sketch, "E89.MirrorCS", {"start": v(15, -120) * mm, "mid": v(0, -135) * mm, "end": v(-15, -120) * mm});
            skLineSegment(sketch, "E90.MirrorCS", {"start": v(15, -108) * mm, "end": v(15, -120) * mm});
            skLineSegment(sketch, "E91.MirrorCS", {"start": v(33, -90) * mm, "end": v(15, -108) * mm});
            skCircle(sketch, "E92.MirrorC", {"center": v(0, -120) * mm, "radius": 6 * mm});
            skLineSegment(sketch, "E93.MirrorCS", {"start": v(0, -90) * mm, "end": v(0, -120) * mm, "construction": true});
            skSolve(sketch);
        }
        {
            var Q0;
            Q0=makeQuery(id+"F16.imprint","IMPRINT",FACE,{"disambiguationData":[TD([[makeQuery(id+"F16.imprint","IMPRINT",EDGE,{"derivedFrom":sQuery(id+"F16.wireOp",EDGE,"E88.MirrorCS")}),1.0]])]});
            var Q1;
            Q1=makeQuery(id+"F16.imprint","IMPRINT",FACE,{"disambiguationData":[TD([[makeQuery(id+"F16.imprint","IMPRINT",EDGE,{"derivedFrom":makeQuery(id+"F1.opExtrude","CAP_EDGE",EDGE,{"disambiguationData":[OSD([sQuery(id+"F0.wireOp",EDGE,"E1.left")])],"isStart":true})}),-1.0]])]});
            var Q2;
            {var subQ1=sQuery(id+"F16.wireOp",EDGE,"E79");Q2=makeQuery(id+"F16.imprint","IMPRINT",FACE,{"disambiguationData":[TD([[makeQuery(id+"F16.imprint","IMPRINT",EDGE,{"derivedFrom":subQ1}),-1.0]])]});}
            var Q3;
            Q3=makeQuery(id+"F2.opExtrude","CAP_FACE",FACE,{"disambiguationData":[OSD([sQuery(id+"F0.wireOp",EDGE,"E12"),sQuery(id+"F0.wireOp",EDGE,"E13"),sQuery(id+"F0.wireOp",EDGE,"E14"),sQuery(id+"F0.wireOp",EDGE,"E15"),sQuery(id+"F0.wireOp",EDGE,"E17.filletArc"),sQuery(id+"F0.wireOp",EDGE,"E18.filletArc"),sQuery(id+"F0.wireOp",EDGE,"E19.filletArc"),sQuery(id+"F0.wireOp",EDGE,"E20.filletArc"),sQuery(id+"F0.wireOp",EDGE,"E25.0"),sQuery(id+"F0.wireOp",EDGE,"E25.1"),sQuery(id+"F0.wireOp",EDGE,"E25.2"),sQuery(id+"F0.wireOp",EDGE,"E25.3"),sQuery(id+"F0.wireOp",EDGE,"E25.4"),sQuery(id+"F0.wireOp",EDGE,"E25.5"),sQuery(id+"F0.wireOp",EDGE,"E25.6"),sQuery(id+"F0.wireOp",EDGE,"E25.7")])],"isStart":false});
            extrude(context, id + "F17", {"entities" : qUnion([Q0, Q1, Q2]), "endBound" : BoundingType.UP_TO_SURFACE, "depth" : 25 * mm, "endBoundEntityFace" : qUnion([Q3]), "offsetDistance" : 25 * mm});
        }
    });
